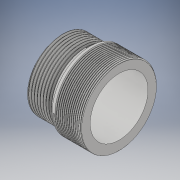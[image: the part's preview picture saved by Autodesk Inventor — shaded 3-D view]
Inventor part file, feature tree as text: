
AUTODESK INVENTOR PART (.ipt)
format: ipt  version: 2019 (Build 230136000, 136)  size: 1,924,608 bytes
history: native  units: mm
features: sketch x3, extrude x2, helix x2, projected_geometry x1
ambient origin geometry x8: Origin, YZ Plane, XZ Plane, XY Plane, X Axis, Y Axis, Z Axis, Center Point
bodies: Body1 (feature_tree)
feature tree (8):
  extrude  "Extrusion2"  Depth=20.0mm
  helix  "Coil1"  [1 undecoded]
  extrude  "Extrusion3"  Depth=1.0mm
  helix  "Coil2"  [1 undecoded]
  sketch  "Sketch2"  dims[d0=24.0mm d3=20.0mm d4=10.0mm d5=0.0mm]
  sketch  "Sketch4"  dims[d6=60.0deg d7=1.0mm d10=60.0deg]
  sketch  "Sketch5"  dims[d11=1.0mm d12=1.0mm d13=10.0mm d14=10.0mm d15=0.0mm d16=90.0deg d17=90.0deg d18=0.0mm d19=0.0mm d20=0.614mm d22=0.144333mm d24=26.289mm d25=10.0mm d26=0.0mm d27=60.0deg d28=0.635mm d29=60.0deg d33=1.0mm d34=10.0mm d35=0.635mm d36=0.555625mm d37=0.15875mm d38=0.635mm d39=10.0mm d40=10.0mm d41=0.0mm d42=90.0deg d43=90.0deg d44=0.0mm d45=0.0mm]
  projected_geometry  "Projected Loop1"
note: 2 required parameter values undecoded (feature->parameter linkage not recoverable at this tier; creation-order binding heuristic only, values carry confidence <= 0.55)
